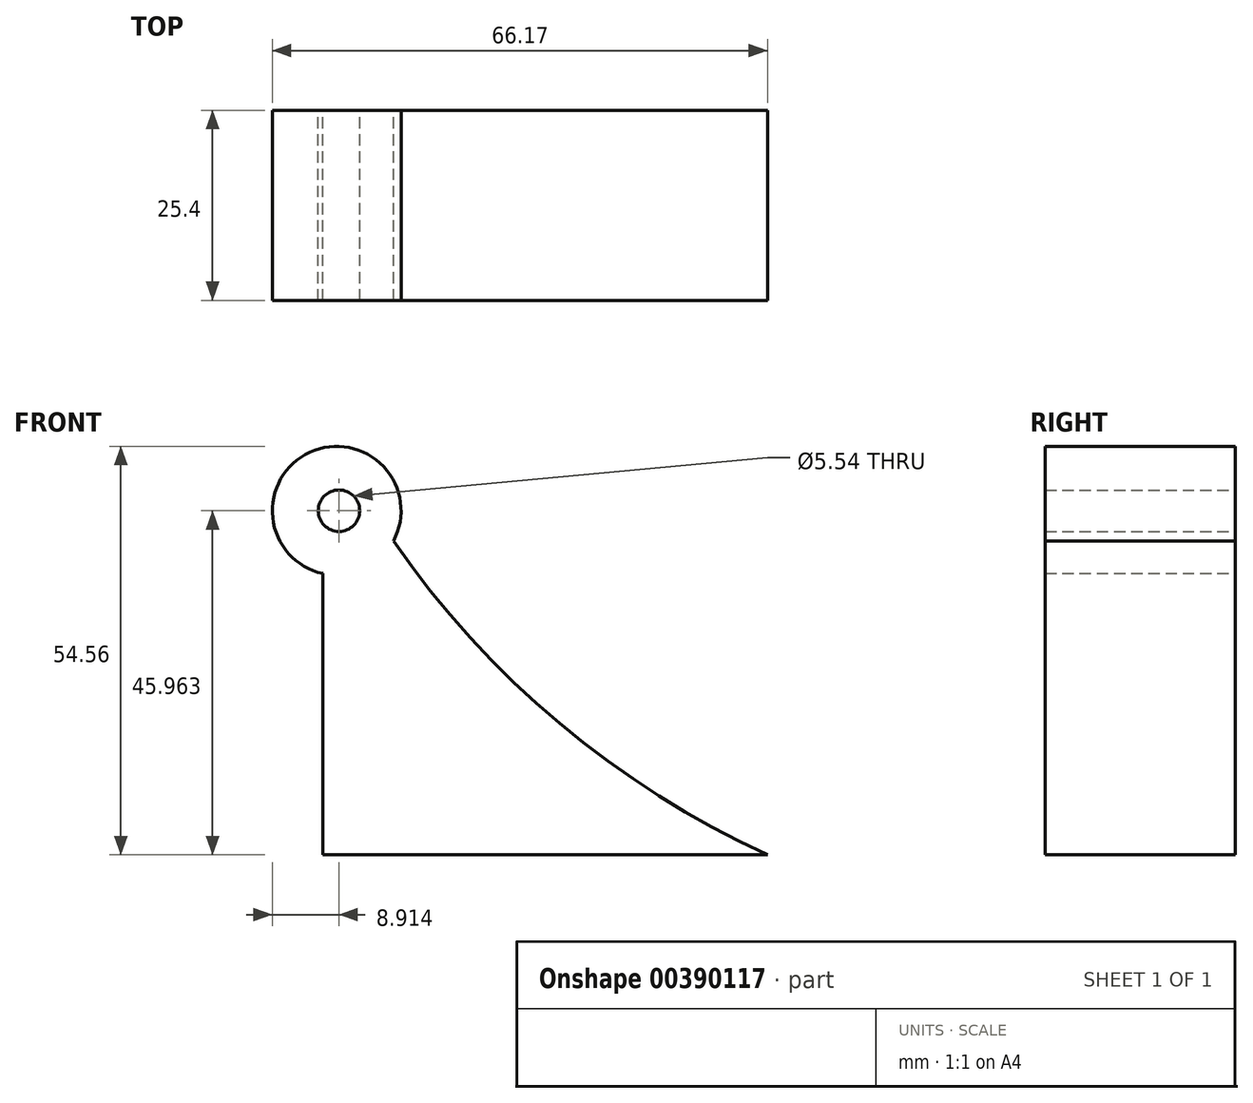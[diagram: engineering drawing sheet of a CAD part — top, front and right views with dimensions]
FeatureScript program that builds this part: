
annotation { "Feature Type Name" : "Feature", "Feature Type Description" : "" }
export const myFeature = defineFeature(function(context is Context, id is Id, definition is map)
    precondition{}
    {
        {
            var Q0;
            Q0=qCreatedBy(makeId("Front.planeOp"),FACE);
            var sketch = newSketch(context, id + "F0", { "sketchPlane" : qUnion([Q0])});
            skLineSegment(sketch, "E0", {"start": v(-2.79, 0) * mm, "end": v(-62.21, 0) * mm});
            skArc(sketch, "E1", {"start": v(-54.15, 43.94) * mm, "mid": v(-31.54, 18.38) * mm, "end": v(-2.79, 0) * mm});
            skCircle(sketch, "E2", {"center": v(-60.36, 45.96) * mm, "radius": 8.6 * mm});
            skLineSegment(sketch, "E3", {"start": v(-62.21, 0) * mm, "end": v(-62.21, 37.57) * mm});
            skSolve(sketch);
        }
        {
            var Q0;
            Q0 = qSketchRegion(id + "F0", true);
            extrude(context, id + "F1", {"entities" : qUnion([Q0]), "depth" : 25.4 * mm});
        }
        {
            var Q0;
            Q0=qCreatedBy(makeId("Front.planeOp"),FACE);
            var sketch = newSketch(context, id + "F2", { "sketchPlane" : qUnion([Q0])});
            skCircle(sketch, "E4", {"center": v(-60.05, 45.96) * mm, "radius": 2.77 * mm});
            skSolve(sketch);
        }
        {
            var Q0;
            Q0 = qSketchRegion(id + "F2", true);
            extrude(context, id + "F3", {"entities" : qUnion([Q0]), "operationType" : NewBodyOperationType.REMOVE, "depth" : 25.4 * mm});
        }
    });
